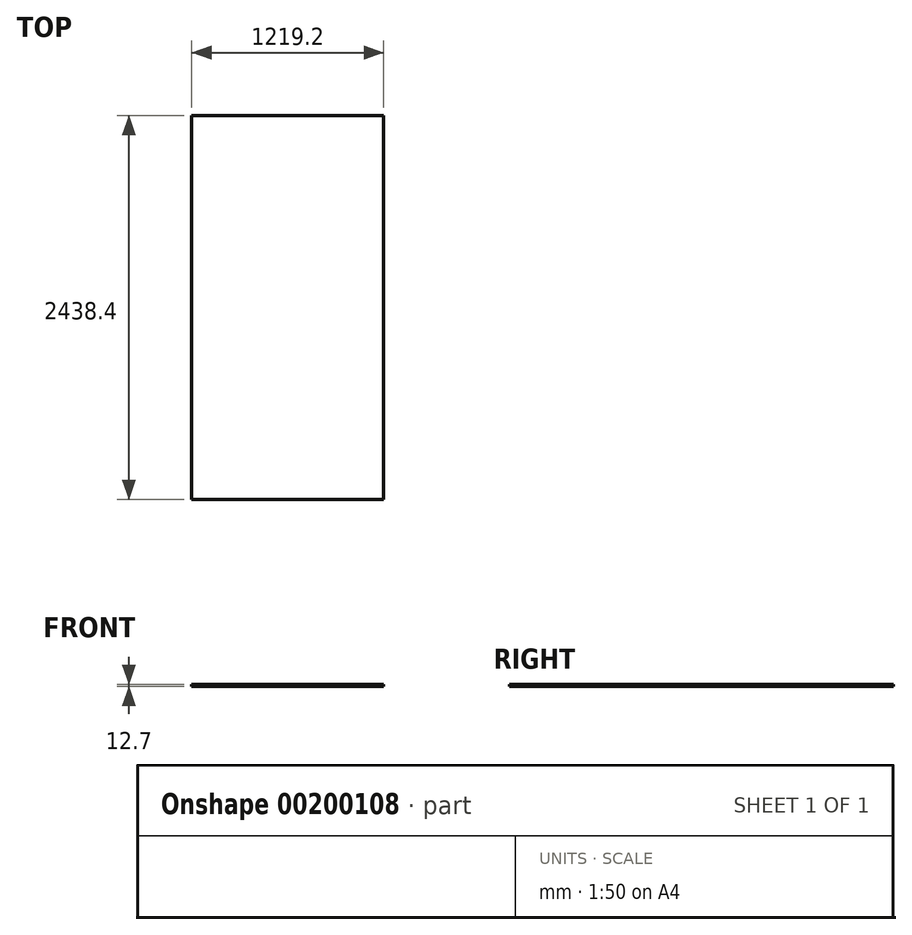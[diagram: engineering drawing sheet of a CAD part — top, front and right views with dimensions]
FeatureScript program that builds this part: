
annotation { "Feature Type Name" : "Feature", "Feature Type Description" : "" }
export const myFeature = defineFeature(function(context is Context, id is Id, definition is map)
    precondition{}
    {
        {
            var Q0;
            Q0=qCreatedBy(makeId("Top.planeOp"),FACE);
            var sketch = newSketch(context, id + "F0", { "sketchPlane" : qUnion([Q0])});
            skLineSegment(sketch, "E0.bottom", {"start": v(-609.6, 1219.2) * mm, "end": v(609.6, 1219.2) * mm});
            skLineSegment(sketch, "E0.top", {"start": v(-609.6, -1219.2) * mm, "end": v(609.6, -1219.2) * mm});
            skLineSegment(sketch, "E0.left", {"start": v(-609.6, 1219.2) * mm, "end": v(-609.6, -1219.2) * mm});
            skLineSegment(sketch, "E0.right", {"start": v(609.6, 1219.2) * mm, "end": v(609.6, -1219.2) * mm});
            skPoint(sketch, "E0.middle", {"position": v(0, 0) * mm});
            skSolve(sketch);
        }
        {
            var Q0;
            Q0 = qSketchRegion(id + "F0", true);
            extrude(context, id + "F1", {"entities" : qUnion([Q0]), "depth" : 12.7 * mm});
        }
    });
